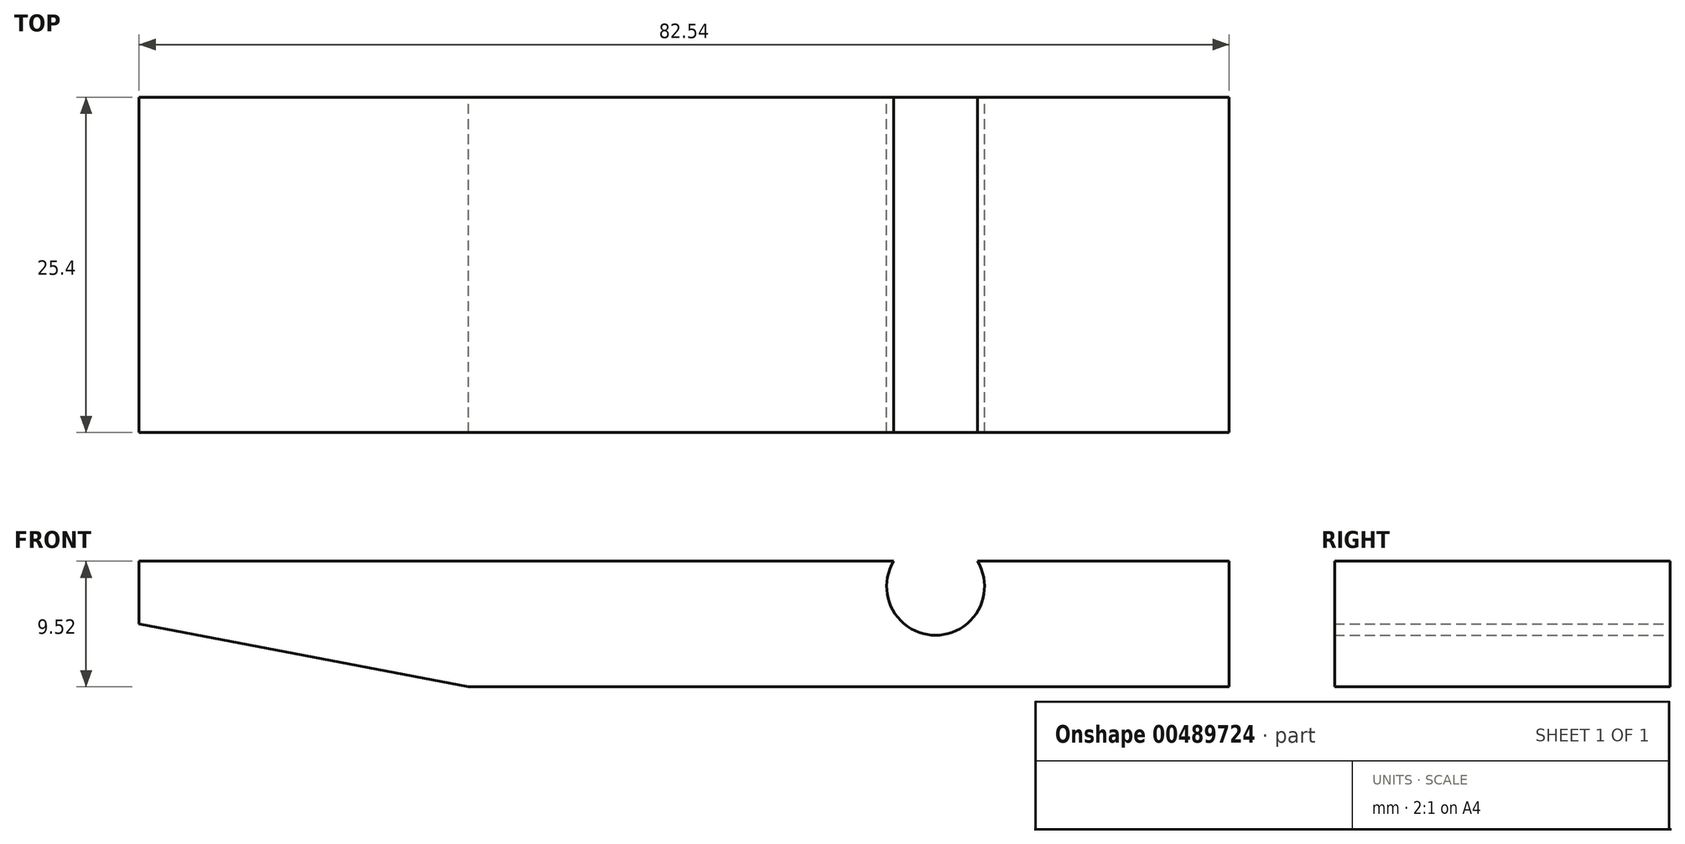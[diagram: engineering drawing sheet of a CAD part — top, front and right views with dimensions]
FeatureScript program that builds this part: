
annotation { "Feature Type Name" : "Feature", "Feature Type Description" : "" }
export const myFeature = defineFeature(function(context is Context, id is Id, definition is map)
    precondition{}
    {
        {
            var Q0;
            Q0=qCreatedBy(makeId("Front.planeOp"),FACE);
            var sketch = newSketch(context, id + "F0", { "sketchPlane" : qUnion([Q0])});
            skLineSegment(sketch, "E0.bottom", {"start": v(41.28, -4.76) * mm, "end": v(-16.33, -4.76) * mm});
            skLineSegment(sketch, "E0.top", {"start": v(41.28, 4.76) * mm, "end": v(22.23, 4.76) * mm});
            skLineSegment(sketch, "E0.left", {"start": v(41.28, -4.76) * mm, "end": v(41.28, 4.76) * mm});
            skLineSegment(sketch, "E0.right", {"start": v(-41.28, 0) * mm, "end": v(-41.28, 4.76) * mm});
            skPoint(sketch, "E0.middle", {"position": v(0, 0) * mm});
            skLineSegment(sketch, "E1", {"start": v(-41.28, 0) * mm, "end": v(-16.33, -4.76) * mm});
            skPoint(sketch, "E2.orphan", {"position": v(-41.28, -4.76) * mm});
            skLineSegment(sketch, "E3.trimOffspring", {"start": v(15.88, 4.76) * mm, "end": v(-41.28, 4.76) * mm});
            skArc(sketch, "E4", {"start": v(15.88, 4.76) * mm, "mid": v(19.05, -0.86) * mm, "end": v(22.23, 4.76) * mm});
            skPoint(sketch, "E5.center.orphan", {"position": v(19.05, 4.76) * mm});
            skSolve(sketch);
        }
        {
            var Q0;
            Q0=makeQuery(id+"F0.imprint","IMPRINT",FACE,{"disambiguationData":[TD([[makeQuery(id+"F0.imprint","IMPRINT",EDGE,{"derivedFrom":sQuery(id+"F0.wireOp",EDGE,"E0.bottom")}),-1.0]])]});
            extrude(context, id + "F1", {"entities" : qUnion([Q0]), "depth" : 25.4 * mm});
        }
    });
